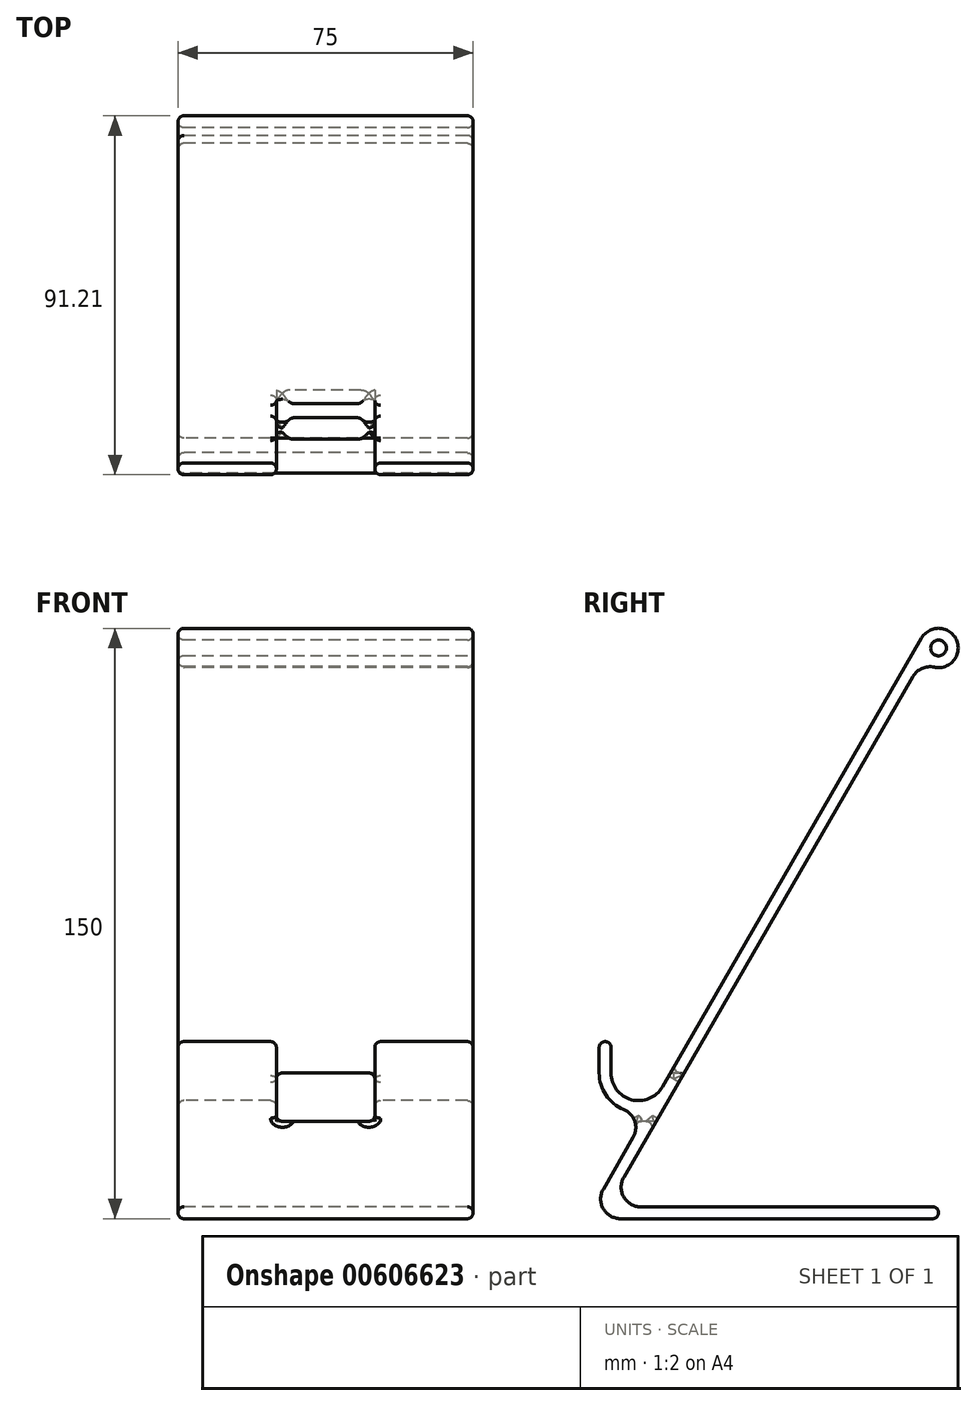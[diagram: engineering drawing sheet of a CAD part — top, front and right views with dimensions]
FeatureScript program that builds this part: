
annotation { "Feature Type Name" : "Feature", "Feature Type Description" : "" }
export const myFeature = defineFeature(function(context is Context, id is Id, definition is map)
    precondition{}
    {
        {
            var Q0;
            Q0=qCreatedBy(makeId("Right.planeOp"),FACE);
            var sketch = newSketch(context, id + "F0", { "sketchPlane" : qUnion([Q0])});
            skLineSegment(sketch, "E0.2", {"start": v(-43.49, -30) * mm, "end": v(-43.49, -38) * mm});
            skArc(sketch, "E0.4", {"start": v(-43.49, -38) * mm, "mid": v(-41.8, -43.57) * mm, "end": v(-37.29, -47.25) * mm});
            skLineSegment(sketch, "E1.2", {"start": v(-40.49, -30) * mm, "end": v(-40.49, -38) * mm});
            skLineSegment(sketch, "E1.3", {"start": v(-27.42, -41.5) * mm, "end": v(38.4, 72.5) * mm});
            skArc(sketch, "E2.filletArc", {"start": v(-40.49, -38) * mm, "mid": v(-35.3, -44.76) * mm, "end": v(-27.42, -41.5) * mm});
            skLineSegment(sketch, "E3", {"start": v(-43.49, -30) * mm, "end": v(-40.49, -30) * mm});
            skLineSegment(sketch, "E4", {"start": v(-42.44, -67.5) * mm, "end": v(-34.86, -54.37) * mm});
            skLineSegment(sketch, "E5.bottom", {"start": v(-38.1, -75) * mm, "end": v(42.72, -75) * mm});
            skLineSegment(sketch, "E5.top", {"start": v(-32.9, -72) * mm, "end": v(42.72, -72) * mm});
            skLineSegment(sketch, "E5.right", {"start": v(42.72, -75) * mm, "end": v(42.72, -72) * mm});
            skLineSegment(sketch, "E6", {"start": v(-37.24, -64.5) * mm, "end": v(36.22, 62.74) * mm});
            skPoint(sketch, "E7", {"position": v(0, 0) * mm});
            skArc(sketch, "E8", {"start": v(38.4, 72.5) * mm, "mid": v(47.3, 72.01) * mm, "end": v(41.64, 65.12) * mm});
            skPoint(sketch, "E9.visualSharp", {"position": v(-31, -47.68) * mm});
            skArc(sketch, "E9.filletArc", {"start": v(-34.86, -54.37) * mm, "mid": v(-34.45, -50.26) * mm, "end": v(-37.29, -47.25) * mm});
            skArc(sketch, "E10.filletArc", {"start": v(-37.24, -64.5) * mm, "mid": v(-37.24, -69.5) * mm, "end": v(-32.9, -72) * mm});
            skArc(sketch, "E11.filletArc", {"start": v(-42.44, -67.5) * mm, "mid": v(-42.44, -72.5) * mm, "end": v(-38.1, -75) * mm});
            skArc(sketch, "E12", {"start": v(41.64, 65.12) * mm, "mid": v(38.54, 64.82) * mm, "end": v(36.22, 62.74) * mm});
            skCircle(sketch, "E13", {"center": v(42.72, 70) * mm, "radius": 2 * mm});
            skSolve(sketch);
        }
        {
            var Q0;
            Q0=qSketchRegion(id+"F0",true);
            extrude(context, id + "F1", {"entities" : qUnion([Q0]), "endBound" : BoundingType.SYMMETRIC, "depth" : 75 * mm, "offsetDistance" : 25 * mm});
        }
        {
            var Q0;
            Q0=makeQuery(id+"F1.opExtrude","SWEPT_FACE",FACE,{"disambiguationData":[OSD([sQuery(id+"F0.wireOp",EDGE,"E0.2")])]});
            var sketch = newSketch(context, id + "F2", { "sketchPlane" : qUnion([Q0])});
            skLineSegment(sketch, "E14.bottom", {"start": v(-12.5, -38) * mm, "end": v(12.5, -38) * mm});
            skLineSegment(sketch, "E14.top", {"start": v(-12.5, -50.25) * mm, "end": v(12.5, -50.25) * mm});
            skLineSegment(sketch, "E14.left", {"start": v(-12.5, -38) * mm, "end": v(-12.5, -50.25) * mm});
            skLineSegment(sketch, "E14.right", {"start": v(12.5, -38) * mm, "end": v(12.5, -50.25) * mm});
            skSolve(sketch);
        }
        {
            var Q0;
            Q0=qSketchRegion(id+"F2",true);
            extrude(context, id + "F3", {"entities" : qUnion([Q0]), "operationType" : NewBodyOperationType.REMOVE, "oppositeDirection" : true, "depth" : 25 * mm, "offsetDistance" : 25 * mm});
        }
        {
            var Q0;
            Q0=makeQuery(id+"F1.opExtrude","SWEPT_FACE",FACE,{"disambiguationData":[OSD([sQuery(id+"F0.wireOp",EDGE,"E0.2")])]});
            var sketch = newSketch(context, id + "F4", { "sketchPlane" : qUnion([Q0])});
            skLineSegment(sketch, "E15.bottom", {"start": v(-12.5, -38) * mm, "end": v(12.5, -38) * mm});
            skLineSegment(sketch, "E15.top", {"start": v(-12.5, -25.3) * mm, "end": v(12.5, -25.3) * mm});
            skLineSegment(sketch, "E15.left", {"start": v(-12.5, -38) * mm, "end": v(-12.5, -25.3) * mm});
            skLineSegment(sketch, "E15.right", {"start": v(12.5, -38) * mm, "end": v(12.5, -25.3) * mm});
            skSolve(sketch);
        }
        {
            var Q0;
            Q0 = qSketchRegion(id + "F4", true);
            extrude(context, id + "F5", {"entities" : qUnion([Q0]), "operationType" : NewBodyOperationType.REMOVE, "oppositeDirection" : true, "depth" : 5 * mm, "offsetDistance" : 25 * mm});
        }
        {
            var Q0;
            Q0=makeQuery(id+"F1.opExtrude","SWEPT_FACE",FACE,{"disambiguationData":[OSD([sQuery(id+"F0.wireOp",EDGE,"E3")])]});
            var Q1;
            Q1=makeQuery(id+"F1.opExtrude","CAP_FACE",FACE,{"disambiguationData":[OSD([sQuery(id+"F0.wireOp",EDGE,"E0.2"),sQuery(id+"F0.wireOp",EDGE,"E0.4"),sQuery(id+"F0.wireOp",EDGE,"E1.2"),sQuery(id+"F0.wireOp",EDGE,"E1.3"),sQuery(id+"F0.wireOp",EDGE,"E2.filletArc"),sQuery(id+"F0.wireOp",EDGE,"E3"),sQuery(id+"F0.wireOp",EDGE,"OJqH4mra-1SRE-s8op-VV3v-gDYp8EEXXtRn"),sQuery(id+"F0.wireOp",EDGE,"E4"),sQuery(id+"F0.wireOp",EDGE,"E5.bottom"),sQuery(id+"F0.wireOp",EDGE,"E5.top"),sQuery(id+"F0.wireOp",EDGE,"E5.right"),sQuery(id+"F0.wireOp",EDGE,"E6"),sQuery(id+"F0.wireOp",EDGE,"E8"),sQuery(id+"F0.wireOp",EDGE,"jVerfQlz-GGoS-WxWe-SnGt-XEWwIJdHr9bm"),sQuery(id+"F0.wireOp",EDGE,"E9.filletArc"),sQuery(id+"F0.wireOp",EDGE,"E10.filletArc"),sQuery(id+"F0.wireOp",EDGE,"E11.filletArc")])],"isStart":false});
            var Q2;
            Q2=makeQuery(id+"F1.opExtrude","CAP_FACE",FACE,{"disambiguationData":[OSD([sQuery(id+"F0.wireOp",EDGE,"E0.2"),sQuery(id+"F0.wireOp",EDGE,"E0.4"),sQuery(id+"F0.wireOp",EDGE,"E1.2"),sQuery(id+"F0.wireOp",EDGE,"E1.3"),sQuery(id+"F0.wireOp",EDGE,"E2.filletArc"),sQuery(id+"F0.wireOp",EDGE,"E3"),sQuery(id+"F0.wireOp",EDGE,"OJqH4mra-1SRE-s8op-VV3v-gDYp8EEXXtRn"),sQuery(id+"F0.wireOp",EDGE,"E4"),sQuery(id+"F0.wireOp",EDGE,"E5.bottom"),sQuery(id+"F0.wireOp",EDGE,"E5.top"),sQuery(id+"F0.wireOp",EDGE,"E5.right"),sQuery(id+"F0.wireOp",EDGE,"E6"),sQuery(id+"F0.wireOp",EDGE,"E8"),sQuery(id+"F0.wireOp",EDGE,"jVerfQlz-GGoS-WxWe-SnGt-XEWwIJdHr9bm"),sQuery(id+"F0.wireOp",EDGE,"E9.filletArc"),sQuery(id+"F0.wireOp",EDGE,"E10.filletArc"),sQuery(id+"F0.wireOp",EDGE,"E11.filletArc")])],"isStart":true});
            var Q3;
            Q3=makeQuery(id+"F1.opExtrude","SWEPT_FACE",FACE,{"disambiguationData":[OSD([sQuery(id+"F0.wireOp",EDGE,"E5.right")])]});
            var Q4;
            Q4=makeQuery(id+"F1.opExtrude","SWEPT_EDGE",EDGE,{"disambiguationData":[OSD([sQuery(id+"F0.wireOp",EDGE,"OJqH4mra-1SRE-s8op-VV3v-gDYp8EEXXtRn"),sQuery(id+"F0.wireOp",EDGE,"E8")])]});
            var Q5;
            Q5=makeQuery(id+"F1.opExtrude","SWEPT_EDGE",EDGE,{"disambiguationData":[OSD([sQuery(id+"F0.wireOp",EDGE,"OJqH4mra-1SRE-s8op-VV3v-gDYp8EEXXtRn"),sQuery(id+"F0.wireOp",EDGE,"jVerfQlz-GGoS-WxWe-SnGt-XEWwIJdHr9bm")])]});
            fillet(context, id + "F6", {"entities" : qUnion([Q0, Q1, Q2, Q3, Q4, Q5]), "radius" : 1.5 * mm, "tangentPropagation" : true, "allowEdgeOverflow" : false});
        }
        {
            var Q0;
            Q0=makeQuery(id+"F5.boolean.opBoolean","MERGE",FACE,{"derivedFrom":[makeQuery(id+"F3.boolean.opBoolean","COPY",FACE,{"derivedFrom":makeQuery(id+"F3.opExtrude","SWEPT_FACE",FACE,{"disambiguationData":[OSD([sQuery(id+"F2.wireOp",EDGE,"E14.left")])]})})],"fromTools":[makeQuery(id+"F5.opExtrude","SWEPT_FACE",FACE,{"disambiguationData":[OSD([sQuery(id+"F4.wireOp",EDGE,"E15.left")])]})]});
            var Q1;
            Q1=makeQuery(id+"F5.boolean.opBoolean","MERGE",FACE,{"derivedFrom":[makeQuery(id+"F3.boolean.opBoolean","COPY",FACE,{"derivedFrom":makeQuery(id+"F3.opExtrude","SWEPT_FACE",FACE,{"disambiguationData":[OSD([sQuery(id+"F2.wireOp",EDGE,"E14.right")])]})})],"fromTools":[makeQuery(id+"F5.opExtrude","SWEPT_FACE",FACE,{"disambiguationData":[OSD([sQuery(id+"F4.wireOp",EDGE,"E15.right")])]})]});
            fillet(context, id + "F7", {"entities" : qUnion([Q0, Q1]), "radius" : 1.5 * mm, "tangentPropagation" : true, "allowEdgeOverflow" : false});
        }
    });
